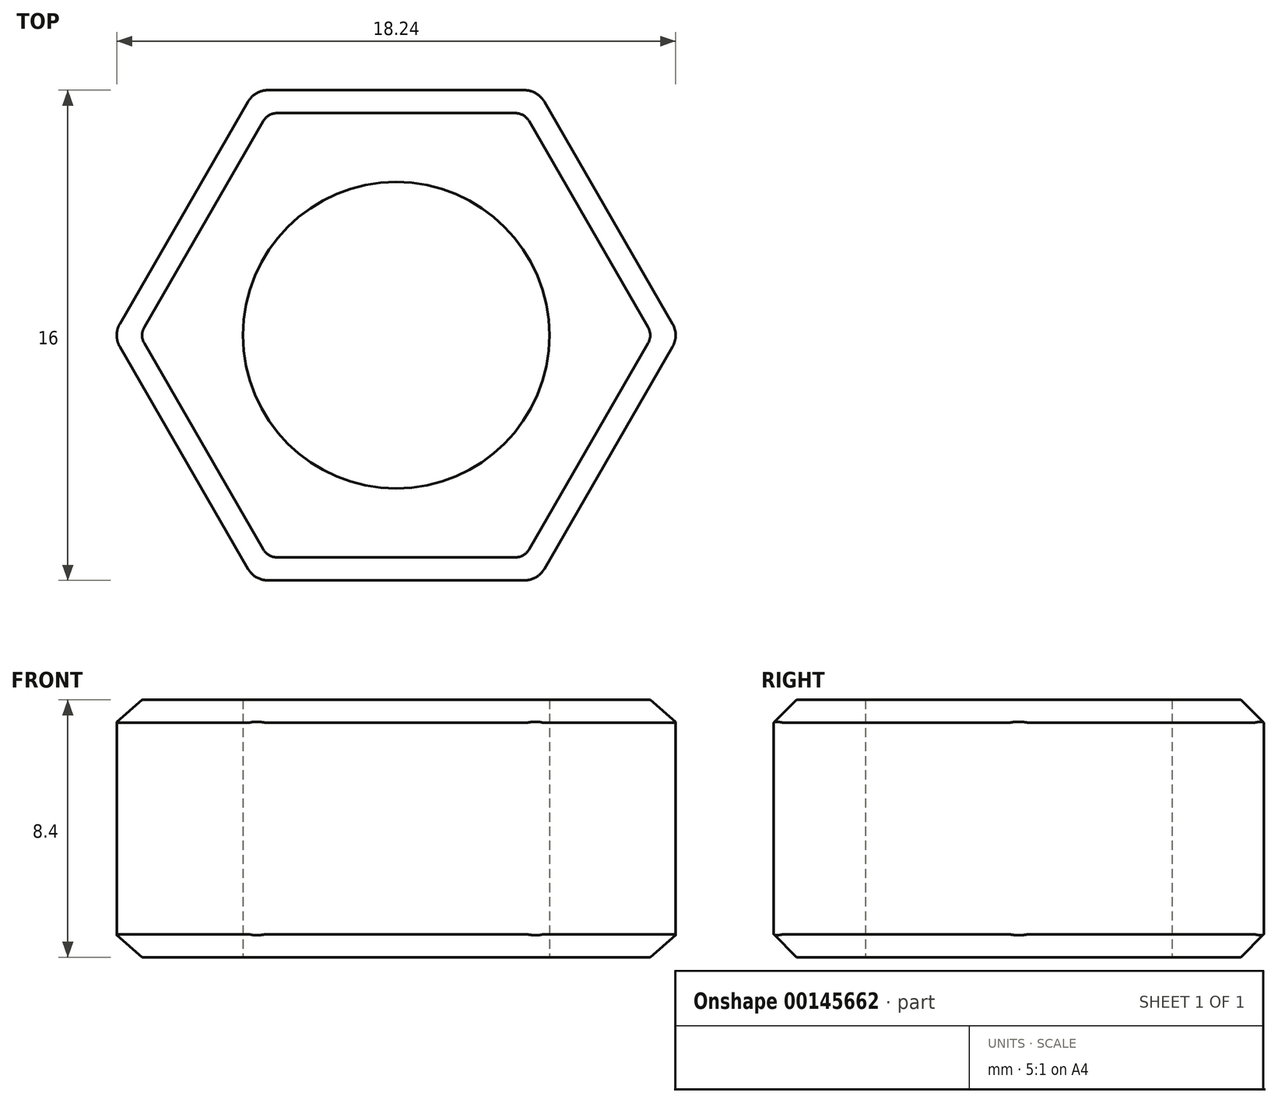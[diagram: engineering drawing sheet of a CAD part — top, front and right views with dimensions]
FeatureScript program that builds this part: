
annotation { "Feature Type Name" : "Feature", "Feature Type Description" : "" }
export const myFeature = defineFeature(function(context is Context, id is Id, definition is map)
    precondition{}
    {
        {
            var Q0;
            Q0=qCreatedBy(makeId("Top.planeOp"),FACE);
            var sketch = newSketch(context, id + "F0", { "sketchPlane" : qUnion([Q0])});
            skCircle(sketch, "E0.cCircle", {"center": v(0, 0) * mm, "radius": 8 * mm, "construction": true});
            skLineSegment(sketch, "E0.0", {"start": v(-4.62, 8) * mm, "end": v(4.62, 8) * mm});
            skLineSegment(sketch, "E0.1", {"start": v(4.62, 8) * mm, "end": v(9.24, 0) * mm});
            skLineSegment(sketch, "E0.2", {"start": v(9.24, 0) * mm, "end": v(4.62, -8) * mm});
            skLineSegment(sketch, "E0.3", {"start": v(4.62, -8) * mm, "end": v(-4.62, -8) * mm});
            skLineSegment(sketch, "E0.4", {"start": v(-4.62, -8) * mm, "end": v(-9.24, 0) * mm});
            skLineSegment(sketch, "E0.5", {"start": v(-9.24, 0) * mm, "end": v(-4.62, 8) * mm});
            skPoint(sketch, "E0.0.midPoint", {"position": v(0, 8) * mm});
            skCircle(sketch, "E1", {"center": v(0, 0) * mm, "radius": 5 * mm});
            skSolve(sketch);
        }
        {
            var Q0;
            Q0 = qSketchRegion(id + "F0", true);
            extrude(context, id + "F1", {"entities" : qUnion([Q0]), "depth" : 8.4 * mm});
        }
        {
            var Q0;
            Q0=makeQuery(id+"F1.opExtrude","CAP_EDGE",EDGE,{"disambiguationData":[OSD([sQuery(id+"F0.wireOp",EDGE,"E0.3")])],"isStart":false});
            var Q1;
            Q1=makeQuery(id+"F1.opExtrude","CAP_EDGE",EDGE,{"disambiguationData":[OSD([sQuery(id+"F0.wireOp",EDGE,"E0.4")])],"isStart":false});
            var Q2;
            Q2=makeQuery(id+"F1.opExtrude","CAP_EDGE",EDGE,{"disambiguationData":[OSD([sQuery(id+"F0.wireOp",EDGE,"E0.5")])],"isStart":false});
            var Q3;
            Q3=makeQuery(id+"F1.opExtrude","CAP_EDGE",EDGE,{"disambiguationData":[OSD([sQuery(id+"F0.wireOp",EDGE,"E0.0")])],"isStart":false});
            var Q4;
            Q4=makeQuery(id+"F1.opExtrude","CAP_EDGE",EDGE,{"disambiguationData":[OSD([sQuery(id+"F0.wireOp",EDGE,"E0.1")])],"isStart":false});
            var Q5;
            Q5=makeQuery(id+"F1.opExtrude","CAP_EDGE",EDGE,{"disambiguationData":[OSD([sQuery(id+"F0.wireOp",EDGE,"E0.2")])],"isStart":false});
            var Q6;
            Q6=makeQuery(id+"F1.opExtrude","CAP_EDGE",EDGE,{"disambiguationData":[OSD([sQuery(id+"F0.wireOp",EDGE,"E0.2")])],"isStart":true});
            var Q7;
            Q7=makeQuery(id+"F1.opExtrude","CAP_EDGE",EDGE,{"disambiguationData":[OSD([sQuery(id+"F0.wireOp",EDGE,"E0.3")])],"isStart":true});
            var Q8;
            Q8=makeQuery(id+"F1.opExtrude","CAP_EDGE",EDGE,{"disambiguationData":[OSD([sQuery(id+"F0.wireOp",EDGE,"E0.4")])],"isStart":true});
            var Q9;
            Q9=makeQuery(id+"F1.opExtrude","CAP_EDGE",EDGE,{"disambiguationData":[OSD([sQuery(id+"F0.wireOp",EDGE,"E0.5")])],"isStart":true});
            var Q10;
            Q10=makeQuery(id+"F1.opExtrude","CAP_EDGE",EDGE,{"disambiguationData":[OSD([sQuery(id+"F0.wireOp",EDGE,"E0.0")])],"isStart":true});
            var Q11;
            Q11=makeQuery(id+"F1.opExtrude","CAP_EDGE",EDGE,{"disambiguationData":[OSD([sQuery(id+"F0.wireOp",EDGE,"E0.1")])],"isStart":true});
            chamfer(context, id + "F2", {"entities" : qUnion([Q0, Q1, Q2, Q3, Q4, Q5, Q6, Q7, Q8, Q9, Q10, Q11]), "width" : 0.75 * mm, "tangentPropagation" : true});
        }
        {
            var Q0;
            Q0=makeQuery(id+"F1.opExtrude","SWEPT_EDGE",EDGE,{"disambiguationData":[OSD([sQuery(id+"F0.wireOp",EDGE,"E0.3"),sQuery(id+"F0.wireOp",EDGE,"E0.4")])]});
            var Q1;
            Q1=makeQuery(id+"F1.opExtrude","SWEPT_EDGE",EDGE,{"disambiguationData":[OSD([sQuery(id+"F0.wireOp",EDGE,"E0.2"),sQuery(id+"F0.wireOp",EDGE,"E0.3")])]});
            var Q2;
            Q2=makeQuery(id+"F2.opChamfer","BLEND_EDGE",EDGE,{"blendedFrom":[makeQuery(id+"F1.opExtrude","CAP_EDGE",EDGE,{"disambiguationData":[OSD([sQuery(id+"F0.wireOp",EDGE,"E0.3")])],"isStart":false}),makeQuery(id+"F1.opExtrude","CAP_EDGE",EDGE,{"disambiguationData":[OSD([sQuery(id+"F0.wireOp",EDGE,"E0.4")])],"isStart":false})],"blendedInto":[]});
            var Q3;
            Q3=makeQuery(id+"F2.opChamfer","BLEND_EDGE",EDGE,{"blendedFrom":[makeQuery(id+"F1.opExtrude","CAP_EDGE",EDGE,{"disambiguationData":[OSD([sQuery(id+"F0.wireOp",EDGE,"E0.2")])],"isStart":false}),makeQuery(id+"F1.opExtrude","CAP_EDGE",EDGE,{"disambiguationData":[OSD([sQuery(id+"F0.wireOp",EDGE,"E0.3")])],"isStart":false})],"blendedInto":[]});
            var Q4;
            Q4=makeQuery(id+"F2.opChamfer","BLEND_EDGE",EDGE,{"blendedFrom":[makeQuery(id+"F1.opExtrude","CAP_EDGE",EDGE,{"disambiguationData":[OSD([sQuery(id+"F0.wireOp",EDGE,"E0.2")])],"isStart":true}),makeQuery(id+"F1.opExtrude","CAP_EDGE",EDGE,{"disambiguationData":[OSD([sQuery(id+"F0.wireOp",EDGE,"E0.3")])],"isStart":true})],"blendedInto":[]});
            var Q5;
            Q5=makeQuery(id+"F2.opChamfer","BLEND_EDGE",EDGE,{"blendedFrom":[makeQuery(id+"F1.opExtrude","CAP_EDGE",EDGE,{"disambiguationData":[OSD([sQuery(id+"F0.wireOp",EDGE,"E0.3")])],"isStart":true}),makeQuery(id+"F1.opExtrude","CAP_EDGE",EDGE,{"disambiguationData":[OSD([sQuery(id+"F0.wireOp",EDGE,"E0.4")])],"isStart":true})],"blendedInto":[]});
            var Q6;
            Q6=makeQuery(id+"F2.opChamfer","BLEND_EDGE",EDGE,{"blendedFrom":[makeQuery(id+"F1.opExtrude","CAP_EDGE",EDGE,{"disambiguationData":[OSD([sQuery(id+"F0.wireOp",EDGE,"E0.4")])],"isStart":false}),makeQuery(id+"F1.opExtrude","CAP_EDGE",EDGE,{"disambiguationData":[OSD([sQuery(id+"F0.wireOp",EDGE,"E0.5")])],"isStart":false})],"blendedInto":[]});
            var Q7;
            Q7=makeQuery(id+"F1.opExtrude","SWEPT_EDGE",EDGE,{"disambiguationData":[OSD([sQuery(id+"F0.wireOp",EDGE,"E0.4"),sQuery(id+"F0.wireOp",EDGE,"E0.5")])]});
            var Q8;
            Q8=makeQuery(id+"F2.opChamfer","BLEND_EDGE",EDGE,{"blendedFrom":[makeQuery(id+"F1.opExtrude","CAP_EDGE",EDGE,{"disambiguationData":[OSD([sQuery(id+"F0.wireOp",EDGE,"E0.4")])],"isStart":true}),makeQuery(id+"F1.opExtrude","CAP_EDGE",EDGE,{"disambiguationData":[OSD([sQuery(id+"F0.wireOp",EDGE,"E0.5")])],"isStart":true})],"blendedInto":[]});
            var Q9;
            Q9=makeQuery(id+"F2.opChamfer","BLEND_EDGE",EDGE,{"blendedFrom":[makeQuery(id+"F1.opExtrude","CAP_EDGE",EDGE,{"disambiguationData":[OSD([sQuery(id+"F0.wireOp",EDGE,"E0.0")])],"isStart":true}),makeQuery(id+"F1.opExtrude","CAP_EDGE",EDGE,{"disambiguationData":[OSD([sQuery(id+"F0.wireOp",EDGE,"E0.5")])],"isStart":true})],"blendedInto":[]});
            var Q10;
            Q10=makeQuery(id+"F1.opExtrude","SWEPT_EDGE",EDGE,{"disambiguationData":[OSD([sQuery(id+"F0.wireOp",EDGE,"E0.0"),sQuery(id+"F0.wireOp",EDGE,"E0.5")])]});
            var Q11;
            Q11=makeQuery(id+"F2.opChamfer","BLEND_EDGE",EDGE,{"blendedFrom":[makeQuery(id+"F1.opExtrude","CAP_EDGE",EDGE,{"disambiguationData":[OSD([sQuery(id+"F0.wireOp",EDGE,"E0.0")])],"isStart":false}),makeQuery(id+"F1.opExtrude","CAP_EDGE",EDGE,{"disambiguationData":[OSD([sQuery(id+"F0.wireOp",EDGE,"E0.5")])],"isStart":false})],"blendedInto":[]});
            var Q12;
            Q12=makeQuery(id+"F2.opChamfer","BLEND_EDGE",EDGE,{"blendedFrom":[makeQuery(id+"F1.opExtrude","CAP_EDGE",EDGE,{"disambiguationData":[OSD([sQuery(id+"F0.wireOp",EDGE,"E0.0")])],"isStart":true}),makeQuery(id+"F1.opExtrude","CAP_EDGE",EDGE,{"disambiguationData":[OSD([sQuery(id+"F0.wireOp",EDGE,"E0.1")])],"isStart":true})],"blendedInto":[]});
            var Q13;
            Q13=makeQuery(id+"F1.opExtrude","SWEPT_EDGE",EDGE,{"disambiguationData":[OSD([sQuery(id+"F0.wireOp",EDGE,"E0.0"),sQuery(id+"F0.wireOp",EDGE,"E0.1")])]});
            var Q14;
            Q14=makeQuery(id+"F2.opChamfer","BLEND_EDGE",EDGE,{"blendedFrom":[makeQuery(id+"F1.opExtrude","CAP_EDGE",EDGE,{"disambiguationData":[OSD([sQuery(id+"F0.wireOp",EDGE,"E0.0")])],"isStart":false}),makeQuery(id+"F1.opExtrude","CAP_EDGE",EDGE,{"disambiguationData":[OSD([sQuery(id+"F0.wireOp",EDGE,"E0.1")])],"isStart":false})],"blendedInto":[]});
            var Q15;
            Q15=makeQuery(id+"F2.opChamfer","BLEND_EDGE",EDGE,{"blendedFrom":[makeQuery(id+"F1.opExtrude","CAP_EDGE",EDGE,{"disambiguationData":[OSD([sQuery(id+"F0.wireOp",EDGE,"E0.1")])],"isStart":true}),makeQuery(id+"F1.opExtrude","CAP_EDGE",EDGE,{"disambiguationData":[OSD([sQuery(id+"F0.wireOp",EDGE,"E0.2")])],"isStart":true})],"blendedInto":[]});
            var Q16;
            Q16=makeQuery(id+"F1.opExtrude","SWEPT_EDGE",EDGE,{"disambiguationData":[OSD([sQuery(id+"F0.wireOp",EDGE,"E0.1"),sQuery(id+"F0.wireOp",EDGE,"E0.2")])]});
            var Q17;
            Q17=makeQuery(id+"F2.opChamfer","BLEND_EDGE",EDGE,{"blendedFrom":[makeQuery(id+"F1.opExtrude","CAP_EDGE",EDGE,{"disambiguationData":[OSD([sQuery(id+"F0.wireOp",EDGE,"E0.1")])],"isStart":false}),makeQuery(id+"F1.opExtrude","CAP_EDGE",EDGE,{"disambiguationData":[OSD([sQuery(id+"F0.wireOp",EDGE,"E0.2")])],"isStart":false})],"blendedInto":[]});
            fillet(context, id + "F3", {"entities" : qUnion([Q0, Q1, Q2, Q3, Q4, Q5, Q6, Q7, Q8, Q9, Q10, Q11, Q12, Q13, Q14, Q15, Q16, Q17]), "radius" : 0.75 * mm, "tangentPropagation" : true, "allowEdgeOverflow" : false});
        }
    });
